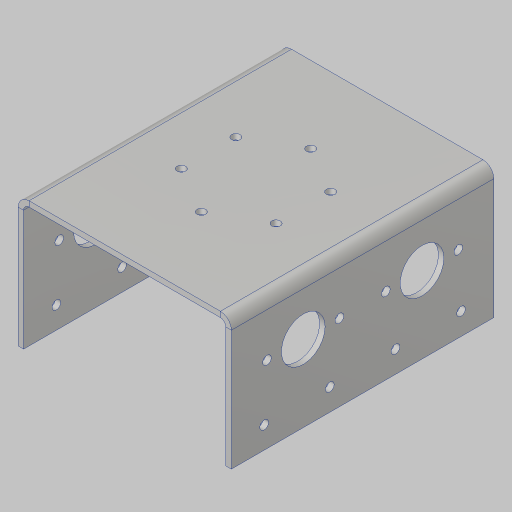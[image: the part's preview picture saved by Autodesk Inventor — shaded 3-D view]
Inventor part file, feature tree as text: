
AUTODESK INVENTOR PART (.ipt)
format: ipt  version: 2023.5 (Build 275446000, 446)  size: 198,144 bytes
history: native  units: in
note: dims shown in document units (in); Inventor stores cm internally (conversion verified against a paired STEP export)
features: sketch x6, sheet_metal_op x4, hole x4, other x2, pattern_circular x1, projected_geometry x1
ambient origin geometry x8: Origin, YZ Plane, XZ Plane, XY Plane, X Axis, Y Axis, Z Axis, Center Point
bodies: Solid1 (feature_tree)
feature tree (18):
  sheet_metal_op  "Face1"
  sheet_metal_op  "Flange1"
  hole  "Hole1"  [1 undecoded]
  hole  "Hole2"  [1 undecoded]
  pattern_circular  "Circular Pattern1"  [2 undecoded]
  hole  "Hole3"  [1 undecoded]
  hole  "Hole4"  [1 undecoded]
  sketch  "Sketch1"  dims[d0=6.0in d1=4.875in]
  other  "Plate1"
  sketch  "Sketch3"  dims[d2=0.125in d4=0.125in]
  other  "Plate2"
  sheet_metal_op  "Bend1"
  sheet_metal_op  "Corner1"
  sketch  "Sketch4"  dims[d5=0.0625in]
  sketch  "Sketch5"  dims[d6=0.25in]
  sketch  "Sketch6"  dims[d7=0.125in]
  sketch  "Sketch7"  dims[d8=3.0in d9=90.0deg d10=0.125in d11=0.5in d12=0.125in d13=0.125in d14=1.25in d15=2.716in d17=1.0in d18=0.38in d19=0.375in d20=0.25in d21=0.5635in d22=0.125in d23=0.0in d24=2.5in d25=0.201in d26=0.75in d27=0.385in d28=0.25in d29=0.5635in d30=0.125in d31=0.8108in d32=2.3622in d33=360.0deg d35=1.5in d36=1.5in d37=1.5in d38=0.5in d39=0.201in d40=0.75in d41=0.385in d42=0.25in d43=0.5635in d44=0.125in d45=0.8108in d46=1.655in d47=1.655in d48=0.201in d49=0.38in d50=0.385in d51=0.25in d52=0.5635in d53=0.125in d54=0.8108in]
  projected_geometry  "Project Cut Edges2"
note: 6 required parameter values undecoded (feature->parameter linkage not recoverable at this tier; creation-order binding heuristic only, values carry confidence <= 0.55)
